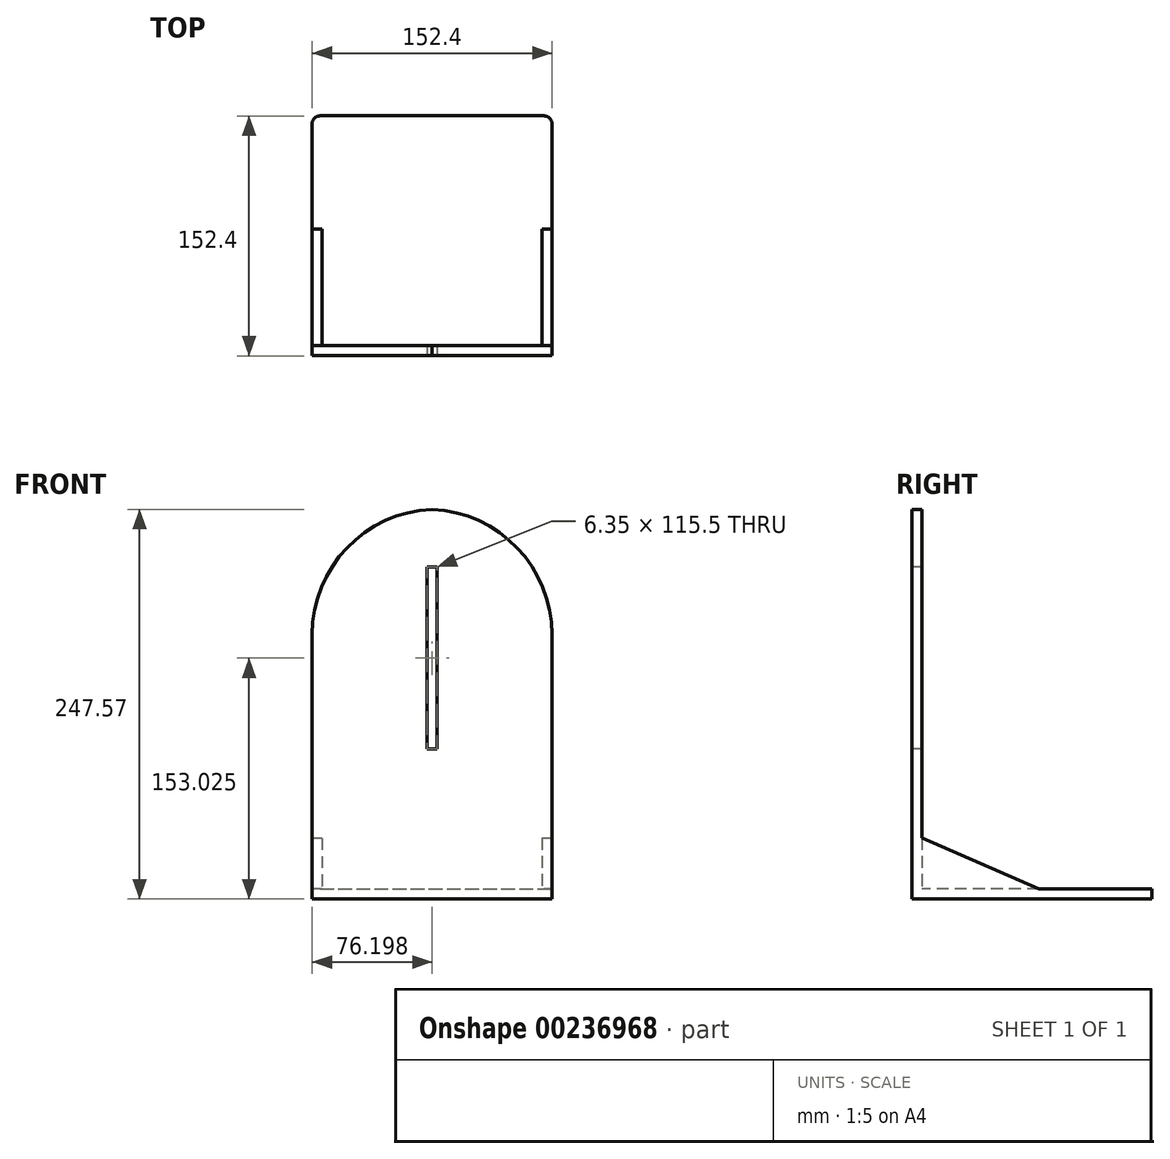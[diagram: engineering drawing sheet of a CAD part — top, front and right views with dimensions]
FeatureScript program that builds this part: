
annotation { "Feature Type Name" : "Feature", "Feature Type Description" : "" }
export const myFeature = defineFeature(function(context is Context, id is Id, definition is map)
    precondition{}
    {
        {
            var Q0;
            Q0=qCreatedBy(makeId("Top.planeOp"),FACE);
            var sketch = newSketch(context, id + "F0", { "sketchPlane" : qUnion([Q0])});
            skLineSegment(sketch, "E0.bottom", {"start": v(-73.45, 71.81) * mm, "end": v(78.95, 71.81) * mm});
            skLineSegment(sketch, "E0.top", {"start": v(-73.45, -80.59) * mm, "end": v(78.95, -80.59) * mm});
            skLineSegment(sketch, "E0.left", {"start": v(-73.45, 71.81) * mm, "end": v(-73.45, -80.59) * mm});
            skLineSegment(sketch, "E0.right", {"start": v(78.95, 71.81) * mm, "end": v(78.95, -80.59) * mm});
            skSolve(sketch);
        }
        {
            var Q0;
            Q0 = qSketchRegion(id + "F0", true);
            extrude(context, id + "F1", {"entities" : qUnion([Q0]), "depth" : 6.35 * mm});
        }
        {
            var Q0;
            Q0=makeQuery(id+"F1.opExtrude","CAP_FACE",FACE,{"disambiguationData":[OSD([sQuery(id+"F0.wireOp",EDGE,"E0.bottom"),sQuery(id+"F0.wireOp",EDGE,"E0.top"),sQuery(id+"F0.wireOp",EDGE,"E0.left"),sQuery(id+"F0.wireOp",EDGE,"E0.right")])],"isStart":false});
            var sketch = newSketch(context, id + "F2", { "sketchPlane" : qUnion([Q0])});
            skLineSegment(sketch, "E1.bottom", {"start": v(-73.45, -74.24) * mm, "end": v(78.95, -74.24) * mm});
            skLineSegment(sketch, "E1.top", {"start": v(-73.45, -80.59) * mm, "end": v(78.95, -80.59) * mm});
            skLineSegment(sketch, "E1.left", {"start": v(-73.45, -74.24) * mm, "end": v(-73.45, -80.59) * mm});
            skLineSegment(sketch, "E1.right", {"start": v(78.95, -74.24) * mm, "end": v(78.95, -80.59) * mm});
            skSolve(sketch);
        }
        {
            var Q0;
            Q0 = qSketchRegion(id + "F2", true);
            extrude(context, id + "F3", {"entities" : qUnion([Q0]), "operationType" : NewBodyOperationType.ADD, "depth" : 241.3 * mm});
        }
        {
            var Q0;
            Q0=makeQuery(id+"F3.boolean.opBoolean","MERGE",FACE,{"derivedFrom":[makeQuery(id+"F1.opExtrude","SWEPT_FACE",FACE,{"disambiguationData":[OSD([sQuery(id+"F0.wireOp",EDGE,"E0.right")])]}),makeQuery(id+"F3.opExtrude","SWEPT_FACE",FACE,{"disambiguationData":[OSD([sQuery(id+"F2.wireOp",EDGE,"E1.right")])]})]});
            var sketch = newSketch(context, id + "F4", { "sketchPlane" : qUnion([Q0])});
            skLineSegment(sketch, "E2", {"start": v(0, 6.35) * mm, "end": v(-74.24, 38.83) * mm});
            skSolve(sketch);
        }
        {
            var Q0;
            Q0=makeQuery(id+"F3.opExtrude","CAP_EDGE",EDGE,{"disambiguationData":[OSD([sQuery(id+"F2.wireOp",EDGE,"E1.left")])],"isStart":false});
            var Q1;
            Q1=makeQuery(id+"F3.opExtrude","CAP_EDGE",EDGE,{"disambiguationData":[OSD([sQuery(id+"F2.wireOp",EDGE,"E1.right")])],"isStart":false});
            fillet(context, id + "F5", {"entities" : qUnion([Q0, Q1]), "radius" : 79.72 * mm, "tangentPropagation" : true, "allowEdgeOverflow" : false});
        }
        {
            var Q0;
            Q0=makeQuery(id+"F3.boolean.opBoolean","MERGE",FACE,{"derivedFrom":[makeQuery(id+"F1.opExtrude","SWEPT_FACE",FACE,{"disambiguationData":[OSD([sQuery(id+"F0.wireOp",EDGE,"E0.top")])]}),makeQuery(id+"F3.opExtrude","SWEPT_FACE",FACE,{"disambiguationData":[OSD([sQuery(id+"F2.wireOp",EDGE,"E1.top")])]})]});
            var sketch = newSketch(context, id + "F6", { "sketchPlane" : qUnion([Q0])});
            skLineSegment(sketch, "E3.bottom", {"start": v(-0.43, 210.77) * mm, "end": v(5.92, 210.77) * mm});
            skLineSegment(sketch, "E3.top", {"start": v(-0.43, 95.27) * mm, "end": v(5.92, 95.27) * mm});
            skLineSegment(sketch, "E3.left", {"start": v(-0.43, 210.77) * mm, "end": v(-0.43, 95.27) * mm});
            skLineSegment(sketch, "E3.right", {"start": v(5.92, 210.77) * mm, "end": v(5.92, 95.27) * mm});
            skSolve(sketch);
        }
        {
            var Q0;
            Q0 = qSketchRegion(id + "F6", true);
            extrude(context, id + "F7", {"entities" : qUnion([Q0]), "operationType" : NewBodyOperationType.REMOVE, "oppositeDirection" : true, "depth" : 25.4 * mm});
        }
        {
            var Q0;
            Q0=makeQuery(id+"F1.opExtrude","SWEPT_EDGE",EDGE,{"disambiguationData":[OSD([sQuery(id+"F0.wireOp",EDGE,"E0.bottom"),sQuery(id+"F0.wireOp",EDGE,"E0.right")])]});
            var Q1;
            Q1=makeQuery(id+"F1.opExtrude","SWEPT_EDGE",EDGE,{"disambiguationData":[OSD([sQuery(id+"F0.wireOp",EDGE,"E0.bottom"),sQuery(id+"F0.wireOp",EDGE,"E0.left")])]});
            fillet(context, id + "F8", {"entities" : qUnion([Q0, Q1]), "radius" : 5.08 * mm, "tangentPropagation" : true, "allowEdgeOverflow" : false});
        }
        {
            var Q0;
            Q0 = qSketchRegion(id + "F4", true);
            var Q1;
            {var subQ0=sQuery(id+"F4.wireOp",EDGE,"E2");Q1=makeQuery(id+"F4.imprint","IMPRINT",FACE,{"disambiguationData":[TD([[makeQuery(id+"F4.imprint","IMPRINT",EDGE,{"derivedFrom":subQ0}),1.0]])]});}
            extrude(context, id + "F9", {"entities" : qUnion([Q0, Q1]), "operationType" : NewBodyOperationType.ADD, "oppositeDirection" : true, "depth" : 6.35 * mm});
        }
        {
            var Q0;
            Q0=makeQuery(id+"F3.boolean.opBoolean","MERGE",FACE,{"derivedFrom":[makeQuery(id+"F1.opExtrude","SWEPT_FACE",FACE,{"disambiguationData":[OSD([sQuery(id+"F0.wireOp",EDGE,"E0.left")])]}),makeQuery(id+"F3.opExtrude","SWEPT_FACE",FACE,{"disambiguationData":[OSD([sQuery(id+"F2.wireOp",EDGE,"E1.left")])]})]});
            var sketch = newSketch(context, id + "F10", { "sketchPlane" : qUnion([Q0])});
            skLineSegment(sketch, "E4", {"start": v(74.24, 38.65) * mm, "end": v(0, 6.35) * mm});
            skSolve(sketch);
        }
        {
            var Q0;
            Q0 = qSketchRegion(id + "F10", true);
            var Q1;
            {var subQ0=sQuery(id+"F10.wireOp",EDGE,"E4");Q1=makeQuery(id+"F10.imprint","IMPRINT",FACE,{"disambiguationData":[TD([[makeQuery(id+"F10.imprint","IMPRINT",EDGE,{"derivedFrom":subQ0}),1.0]])]});}
            extrude(context, id + "F11", {"entities" : qUnion([Q0, Q1]), "operationType" : NewBodyOperationType.ADD, "oppositeDirection" : true, "depth" : 6.35 * mm});
        }
    });
